# Revit family: QF_ELECTROLUXPROFESSIONAL_1LSN0H_TD6-7_G
name_source: partatom
category: Attrezzature speciali
units: mm (PartAtom-declared; Revit-internal decimal feet)

## family parameters
Basato su piano di lavoro = No
Condiviso = No
Punto di calcolo locali = No
Quota connettore circolare = Usa diametro
Sempre verticale = Sì
Taglio con vuoti quando caricato = No
Tipo di parte = Normale

## types (15) — shared parameters
Height Actual = 1050 mm
Latent Heat Output = 0.0
Length Actual = 600 mm  [stored 1.9685 ft]
Modello = TD6-7
Produttore = Electrolux Professional
Sensible Heat Output = 0.0
URL = www.electroluxprofessional.com
Watts = 300 W
Weight = 109
zero-valued in all types: Prospetto di default, Steam Pounds per Hour

## per-type parameters (varying)
| type | Cycle | Depth Actual | Descrizione | Gas KW | Item Number | Phase | Volts |
| 9871830008 | 50 Hz | 875 mm  [stored 2.87073 ft] | TUMBLE DRYER TD6-7 7KG SST DRUM GAS 7KW 230/50/1N COMPASS PRO 6G81 EU SST DO.LEFT.INS. MB DISCON. | 7 | 1LSN20 | 1 | 230 V |
| 9871830052 | 50 Hz | 875 mm  [stored 2.87073 ft] | TUMBLE DRYER TD6-7 7KG GALVA.DRUM GAS 7KW 400/50/3N COMPASS PRO 6G81 EU SILVER DO.LEFT.INS. ELS-NETW. PREP.CB MB DISCON. | 7 | 1L8214 | 3 | 400 V |
| 9871830141 | 50 Hz | 845 mm  [stored 2.77231 ft] | TUMBLE DRYER TD6-7 7KG SST DRUM GAS 7KW 230/50/1N COMPASS PRO 6L80 EU SILVER DO.LEFT EXT.PM. DISCON. 2.I/O | 7 | 1LA23K | 1 | 230 V |
| 9871830117 | 60 Hz | 875 mm  [stored 2.87073 ft] | TUMBLE DRYER TD6-7 7KG GALVA.DRUM GAS 7KW 230/60/1N COMPASS PRO 6G82 EU SILVER DO.LEFT DISCON. | 7 | 1LSNUP | 1 | 230 V |
| 9871830157 | 50 Hz | 845 mm  [stored 2.77231 ft] | TUMBLE DRYER TD6-7 7KG SST DRUM GPL 7KW 200/50/3 COMPASS PRO 6G86 JP SILVER DO.LEFT DISCON. | 0 | 1L0H7G | 3 | 200 V |
| 9871830063 | 60 Hz | 875 mm  [stored 2.87073 ft] | TUMBLE DRYER TD6-7 7KG GALVA.DRUM GAS 7KW 208-240/60/1 COMPASS PRO 6L80 EU SILVER DO.LEFT | 7 | 1L0EKW | 1 | 240 V |
| 9871830053 | 50 Hz | 875 mm  [stored 2.87073 ft] | TUMBLE DRYER TD6-7 7KG GALVA.DRUM GAS 7KW 230/50/1N COMPASS PRO 6G81 EU SILVER DO.LEFT MB DISCON. | 7 | 1L8215 | 1 | 230 V |
| 9871830025 | 50 Hz | 875 mm  [stored 2.87073 ft] | TUMBLE DRYER TD6-7 7KG SST DRUM GAS 7KW 230/50/1N COMPASS PRO 6G81 EU SILVER DO.LEFT MB DISCON. | 7 | 1L0EHX | 1 | 230 V |
| 9871830054 | 50 Hz | 875 mm  [stored 2.87073 ft] | TUMBLE DRYER TD6-7 7KG GALVA.DRUM GAS 7KW 380-415/50/3N COMPASS PRO 6G81 EU SILVER DO.LEFT MB DISCON. | 7 | 1LSN6J | 3 | 415 V |
| 9871830113 | 50 Hz | 875 mm  [stored 2.87073 ft] | TUMBLE DRYER TD6-7 7KG GALVA.DRUM GAS 7KW 230/50/1N COMPASS PRO 6G82 EU SILVER DO.LEFT DISCON. | 7 | 1LSNN0 | 1 | 230 V |
| 9871830138 | 60 Hz | 875 mm  [stored 2.87073 ft] | TUMBLE DRYER TD6-7 7KG GALVA.DRUM GAS 7KW 220/60/3 COMPASS PRO 6G82 EU SILVER DO.LEFT DISCON. | 7 | 1L0GN7 | 3 | 220 V |
| 9871830128 | 50 Hz | 875 mm  [stored 2.87073 ft] | TUMBLE DRYER TD6-7 7KG SST DRUM GAS 7KW 230/50/1N COMPASS PRO 6G81 EU SST DO.LEFT MB DISCON. | 7 | 1L0G99 | 1 | 230 V |
| 9871830118 | 50 Hz | 875 mm  [stored 2.87073 ft] | TUMBLE DRYER TD6-7 7KG GALVA.DRUM GAS 7KW 400/50/3N COMPASS PRO 6G81 SE SILVER DO.LEFT MB DISCON. | 7 | 1LSNWX | 3 | 400 V |
| 9871830156 | 60 Hz | 845 mm  [stored 2.77231 ft] | TUMBLE DRYER TD6-7 7KG GALVA.DRUM GAS 7KW 208-240/60/1 COMPASS PRO 6G82 EU SILVER DO.LEFT DISCON. | 0 | 1LT603 | 1 | 240 V |
| 9871830158 | 60 Hz | 845 mm  [stored 2.77231 ft] | TUMBLE DRYER TD6-7 7KG SST DRUM GPL 7KW 200/60/3 COMPASS PRO 6G86 JP SILVER DO.LEFT DISCON. | 0 | 1L0H7H | 3 | 200 V |

note: [stored X ft] marks values corroborated as IEEE doubles in the binary element streams (Revit-internal decimal feet)

## geometry (parser evidence)
native form markers: Blend x10
no freeform markers — native parametric forms only
